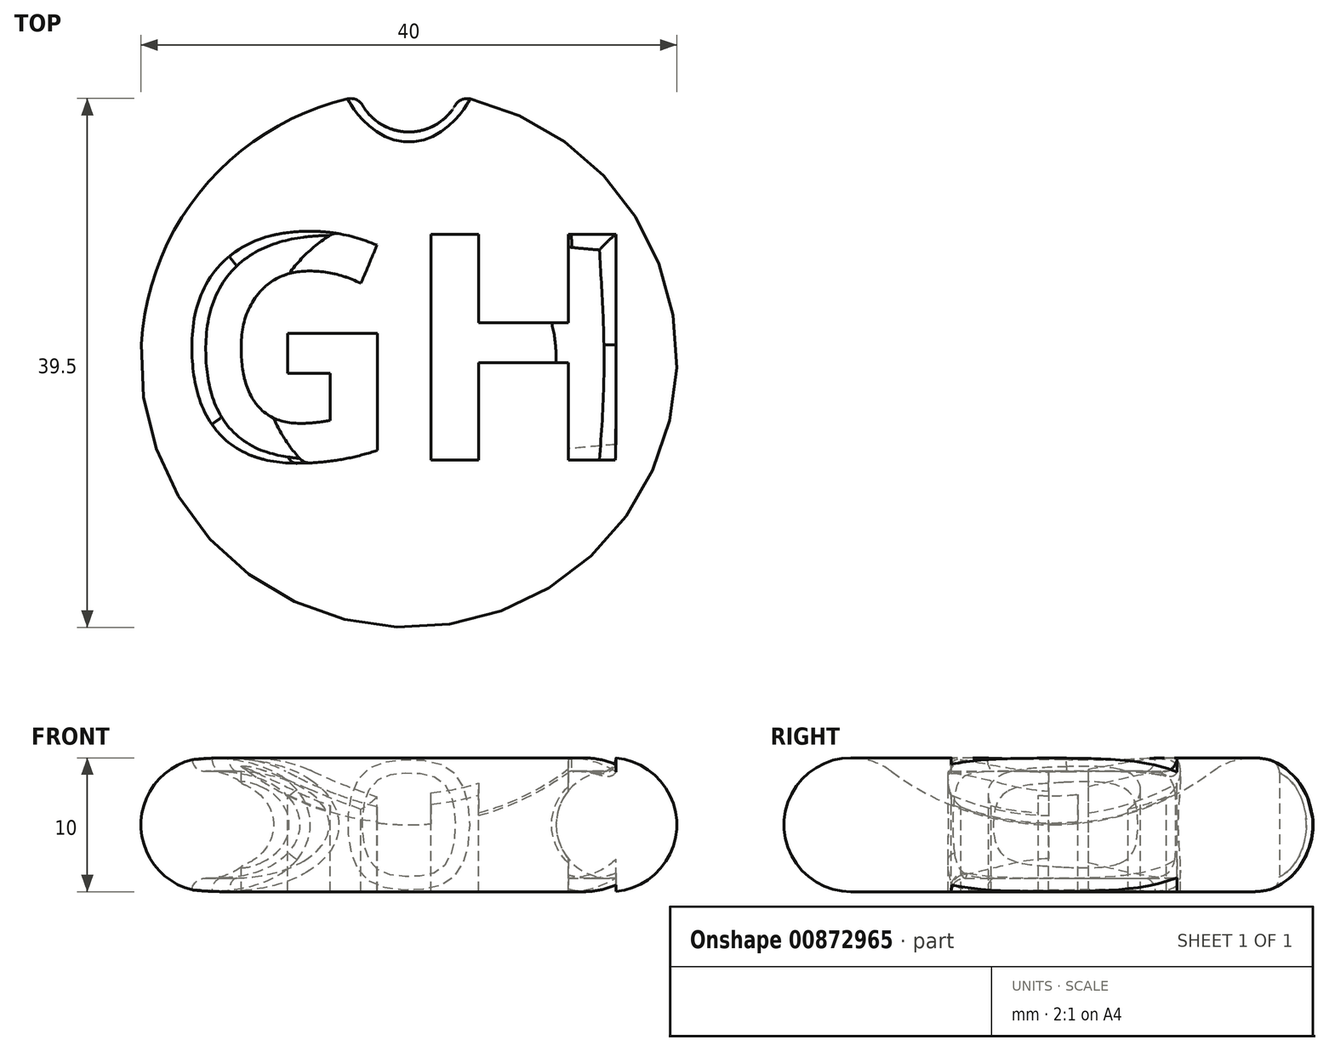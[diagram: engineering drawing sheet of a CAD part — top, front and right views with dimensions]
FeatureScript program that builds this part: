
annotation { "Feature Type Name" : "Feature", "Feature Type Description" : "" }
export const myFeature = defineFeature(function(context is Context, id is Id, definition is map)
    precondition{}
    {
        {
            var Q0;
            Q0=qCreatedBy(makeId("Front.planeOp"),FACE);
            var sketch = newSketch(context, id + "F0", { "sketchPlane" : qUnion([Q0])});
            skArc(sketch, "E0", {"start": v(-12, 9) * mm, "mid": v(-19.74, 6.58) * mm, "end": v(-15, 0) * mm});
            skArc(sketch, "E1", {"start": v(-12, 9) * mm, "mid": v(-6.32, 6.03) * mm, "end": v(0, 5) * mm});
            skLineSegment(sketch, "E2", {"start": v(-15, 0) * mm, "end": v(0, 0) * mm});
            skLineSegment(sketch, "E3", {"start": v(0, 0) * mm, "end": v(0, 5) * mm});
            skSolve(sketch);
        }
        {
            var Q0;
            Q0=makeQuery(id+"F0.imprint","IMPRINT",FACE,{"disambiguationData":[TD([[makeQuery(id+"F0.imprint","IMPRINT",EDGE,{"derivedFrom":sQuery(id+"F0.wireOp",EDGE,"E0")}),1.0]])]});
            var Q1;
            Q1=sQuery(id+"F0.wireOp",EDGE,"E3");
            revolve(context, id + "F1", {"surfaceOperationType" : NewSurfaceOperationType.NEW, "entities" : qUnion([Q0]), "axis" : qUnion([Q1]), "revolveType" : RevolveType.FULL});
        }
        {
            var Q0;
            Q0=qCreatedBy(makeId("Top.planeOp"),FACE);
            cPlane(context, id + "F2", {"entities" : qUnion([Q0]), "cplaneType" : CPlaneType.OFFSET, "offset" : 12 * mm, "width" : 150 * mm, "height" : 150 * mm});
        }
        {
            var Q0;
            Q0=qCreatedBy(id+"F2.planeOp",FACE);
            var sketch = newSketch(context, id + "F3", { "sketchPlane" : qUnion([Q0])});
            skText(sketch, "E4", { "text": "GH", "fontName": "OpenSans-Bold.ttf"});
            const initialGuessF3  = {"E4": [-0.01757, -0.00751, 1, 0, 0.017]};
            skSetInitialGuess(sketch, initialGuessF3);
            skSolve(sketch);
        }
        {
            var Q0;
            Q0 = qSketchRegion(id + "F3", true);
            extrude(context, id + "F4", {"entities" : qUnion([Q0]), "operationType" : NewBodyOperationType.REMOVE, "oppositeDirection" : true, "depth" : 25 * mm, "offsetDistance" : 25 * mm});
        }
        {
            var Q0;
            Q0=qCreatedBy(makeId("Front.planeOp"),FACE);
            var sketch = newSketch(context, id + "F5", { "sketchPlane" : qUnion([Q0])});
            skCircle(sketch, "E5", {"center": v(-15, 5) * mm, "radius": 4 * mm});
            skSolve(sketch);
        }
        {
            var Q0;
            Q0 = qSketchRegion(id + "F5", true);
            var Q1;
            Q1=sQuery(id+"F5.wireOp",EDGE,"E5");
            var Q2;
            Q2=sQuery(id+"F0.wireOp",EDGE,"E3");
            revolve(context, id + "F6", {"operationType" : NewBodyOperationType.ADD, "surfaceOperationType" : NewSurfaceOperationType.NEW, "entities" : qUnion([Q0]), "surfaceEntities" : qUnion([Q1]), "axis" : qUnion([Q2]), "revolveType" : RevolveType.FULL});
        }
        {
            var Q0;
            Q0=qCreatedBy(makeId("Top.planeOp"),FACE);
            var sketch = newSketch(context, id + "F7", { "sketchPlane" : qUnion([Q0])});
            skCircle(sketch, "E6", {"center": v(0, 21) * mm, "radius": 4 * mm});
            skSolve(sketch);
        }
        {
            var Q0;
            Q0 = qSketchRegion(id + "F7", true);
            extrude(context, id + "F8", {"entities" : qUnion([Q0]), "operationType" : NewBodyOperationType.REMOVE, "depth" : 25 * mm, "offsetDistance" : 25 * mm});
        }
        {
            var Q0;
            Q0=makeQuery(id+"F8.boolean.opBoolean","INTERSECT",EDGE,{"derivedFrom":[makeQuery(id+"F4.boolean.opBoolean","SPLIT",FACE,{"disambiguationData":[TD([makeQuery(id+"F1.opRevolve","SWEPT_FACE",FACE,{"disambiguationData":[OSD([sQuery(id+"F0.wireOp",EDGE,"E2")])]})])],"derivedFrom":makeQuery(id+"F1.opRevolve","SWEPT_FACE",FACE,{"disambiguationData":[OSD([sQuery(id+"F0.wireOp",EDGE,"E0")])]})}),makeQuery(id+"F8.opExtrude","SWEPT_FACE",FACE,{"disambiguationData":[OSD([sQuery(id+"F7.wireOp",EDGE,"E6")])]})]});
            fillet(context, id + "F9", {"entities" : qUnion([Q0]), "radius" : 1 * mm, "tangentPropagation" : true, "allowEdgeOverflow" : false});
        }
        {
            var Q0;
            Q0=makeQuery(id+"F6.boolean.opBoolean","INTERSECT",EDGE,{"disambiguationData":[OD(1.0)],"derivedFrom":[makeQuery(id+"F4.boolean.opBoolean","COPY",FACE,{"derivedFrom":makeQuery(id+"F4.opExtrude","SWEPT_FACE",FACE,{"disambiguationData":[OSD([sQuery(id+"F3.wireOp",EDGE,"E4.sketch_text.stroke-6")])]})}),makeQuery(id+"F6.opRevolve","SWEPT_FACE",FACE,{"disambiguationData":[OSD([sQuery(id+"F5.wireOp",EDGE,"E5")])]})]});
            var Q1;
            Q1=makeQuery(id+"F6.boolean.opBoolean","INTERSECT",EDGE,{"disambiguationData":[OD(1.0)],"derivedFrom":[makeQuery(id+"F4.boolean.opBoolean","COPY",FACE,{"derivedFrom":makeQuery(id+"F4.opExtrude","SWEPT_FACE",FACE,{"disambiguationData":[OSD([sQuery(id+"F3.wireOp",EDGE,"E4.sketch_text.stroke-5")])]})}),makeQuery(id+"F6.opRevolve","SWEPT_FACE",FACE,{"disambiguationData":[OSD([sQuery(id+"F5.wireOp",EDGE,"E5")])]})]});
            var Q2;
            Q2=makeQuery(id+"F6.boolean.opBoolean","INTERSECT",EDGE,{"disambiguationData":[OD(1.0)],"derivedFrom":[makeQuery(id+"F4.boolean.opBoolean","COPY",FACE,{"derivedFrom":makeQuery(id+"F4.opExtrude","SWEPT_FACE",FACE,{"disambiguationData":[OSD([sQuery(id+"F3.wireOp",EDGE,"E4.sketch_text.stroke-4")])]})}),makeQuery(id+"F6.opRevolve","SWEPT_FACE",FACE,{"disambiguationData":[OSD([sQuery(id+"F5.wireOp",EDGE,"E5")])]})]});
            var Q3;
            Q3=makeQuery(id+"F6.boolean.opBoolean","INTERSECT",EDGE,{"disambiguationData":[OD(0.0)],"derivedFrom":[makeQuery(id+"F4.boolean.opBoolean","COPY",FACE,{"derivedFrom":makeQuery(id+"F4.opExtrude","SWEPT_FACE",FACE,{"disambiguationData":[OSD([sQuery(id+"F3.wireOp",EDGE,"E4.sketch_text.stroke-7")])]})}),makeQuery(id+"F6.opRevolve","SWEPT_FACE",FACE,{"disambiguationData":[OSD([sQuery(id+"F5.wireOp",EDGE,"E5")])]})]});
            fillet(context, id + "F10", {"entities" : qUnion([Q0, Q1, Q2, Q3]), "radius" : 1 * mm, "tangentPropagation" : true, "allowEdgeOverflow" : false});
        }
        {
            var Q0;
            Q0=makeQuery(id+"F6.boolean.opBoolean","INTERSECT",EDGE,{"disambiguationData":[OD(1.0)],"derivedFrom":[makeQuery(id+"F4.boolean.opBoolean","COPY",FACE,{"derivedFrom":makeQuery(id+"F4.opExtrude","SWEPT_FACE",FACE,{"disambiguationData":[OSD([sQuery(id+"F3.wireOp",EDGE,"E4.sketch_text.stroke-30")])]})}),makeQuery(id+"F6.opRevolve","SWEPT_FACE",FACE,{"disambiguationData":[OSD([sQuery(id+"F5.wireOp",EDGE,"E5")])]})]});
            var Q1;
            Q1=makeQuery(id+"F6.boolean.opBoolean","INTERSECT",EDGE,{"disambiguationData":[OD(1.0)],"derivedFrom":[makeQuery(id+"F4.boolean.opBoolean","COPY",FACE,{"derivedFrom":makeQuery(id+"F4.opExtrude","SWEPT_FACE",FACE,{"disambiguationData":[OSD([sQuery(id+"F3.wireOp",EDGE,"E4.sketch_text.stroke-29")])]})}),makeQuery(id+"F6.opRevolve","SWEPT_FACE",FACE,{"disambiguationData":[OSD([sQuery(id+"F5.wireOp",EDGE,"E5")])]})]});
            var Q2;
            Q2=makeQuery(id+"F6.boolean.opBoolean","INTERSECT",EDGE,{"disambiguationData":[OD(0.0)],"derivedFrom":[makeQuery(id+"F4.boolean.opBoolean","COPY",FACE,{"derivedFrom":makeQuery(id+"F4.opExtrude","SWEPT_FACE",FACE,{"disambiguationData":[OSD([sQuery(id+"F3.wireOp",EDGE,"E4.sketch_text.stroke-19")])]})}),makeQuery(id+"F6.opRevolve","SWEPT_FACE",FACE,{"disambiguationData":[OSD([sQuery(id+"F5.wireOp",EDGE,"E5")])]})]});
            fillet(context, id + "F11", {"entities" : qUnion([Q0, Q1, Q2]), "radius" : 1 * mm, "tangentPropagation" : true, "allowEdgeOverflow" : false});
        }
    });
